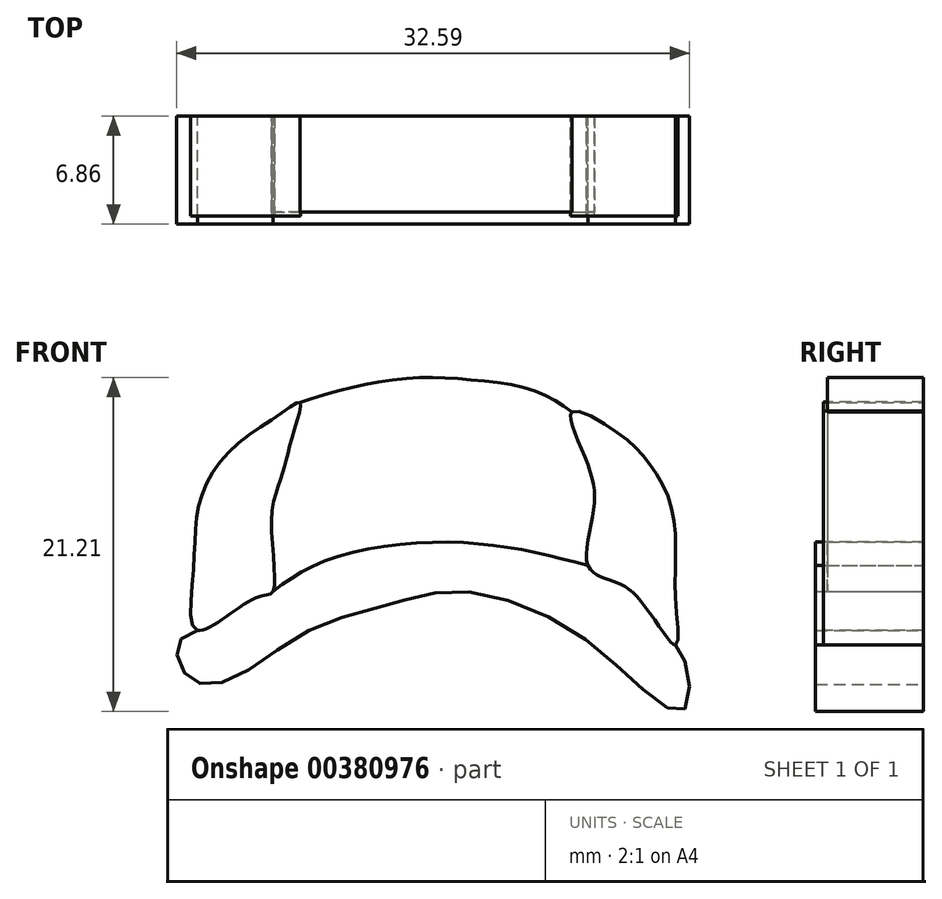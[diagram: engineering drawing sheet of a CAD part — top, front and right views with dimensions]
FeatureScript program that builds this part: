
annotation { "Feature Type Name" : "Feature", "Feature Type Description" : "" }
export const myFeature = defineFeature(function(context is Context, id is Id, definition is map)
    precondition{}
    {
        {
            var Q0;
            Q0=qCreatedBy(makeId("Front.planeOp"),FACE);
            var sketch = newSketch(context, id + "F0", { "sketchPlane" : qUnion([Q0])});
            skFitSpline(sketch, "E0", {"points": [v(-98.95, 24.46) * mm, v(-99.21, 28.23) * mm, v(-98.87, 32.42) * mm, v(-96.9, 35.84) * mm, v(-93.4, 38.41) * mm, v(-92.45, 38.92) * mm, v(-92.96, 36.61) * mm, v(-93.56, 34.39) * mm, v(-94.25, 31.48) * mm, v(-94.16, 26.95) * mm, v(-95.27, 26.52) * mm, v(-98.95, 24.46) * mm]});
            skFitSpline(sketch, "E1", {"points": [v(-75.17, 38.33) * mm, v(-74.23, 35.16) * mm, v(-73.8, 32.08) * mm, v(-74.14, 28.57) * mm, v(-72.69, 27.63) * mm, v(-70.89, 26.43) * mm, v(-68.58, 23.52) * mm, v(-68.58, 26.26) * mm, v(-68.58, 29.6) * mm, v(-69, 32.76) * mm, v(-70.46, 35.33) * mm, v(-72.43, 37.13) * mm, v(-75.17, 38.33) * mm]});
            skFitSpline(sketch, "E2", {"points": [v(-94.16, 26.95) * mm, v(-91, 28.83) * mm, v(-84.84, 30.03) * mm, v(-78.93, 29.68) * mm, v(-74.14, 28.57) * mm], "startDerivative": vector(13.27, 9.67) * mm, "endDerivative": vector(19.14, -5.1) * mm});
            skFitSpline(sketch, "E3", {"points": [v(-75.17, 38.33) * mm, v(-77.56, 39.7) * mm, v(-81.58, 40.38) * mm, v(-85.6, 40.46) * mm, v(-89.97, 39.7) * mm, v(-92.45, 38.92) * mm], "startDerivative": vector(-12.28, 8.74) * mm, "endDerivative": vector(-13.23, -4.52) * mm});
            skFitSpline(sketch, "E4", {"points": [v(-98.95, 24.46) * mm, v(-100.15, 23.7) * mm, v(-100.07, 22.24) * mm, v(-98.95, 21.13) * mm, v(-96.56, 21.47) * mm, v(-91.85, 24.46) * mm, v(-86.8, 26.09) * mm, v(-82.44, 26.95) * mm, v(-75.17, 24.46) * mm, v(-70.12, 20.27) * mm, v(-68.06, 19.42) * mm, v(-67.8, 21.9) * mm, v(-68.58, 23.52) * mm], "startDerivative": vector(-27, -10.61) * mm, "endDerivative": vector(-14.79, 21.62) * mm});
            skSolve(sketch);
        }
        {
            var Q0;
            {var subQ0=sQuery(id+"F0.wireOp",EDGE,"E0");var subQ1=makeQuery(id+"F0.imprint","INTERSECT",VERTEX,{"derivedFrom":[subQ0,sQuery(id+"F0.wireOp",EDGE,"E3")]});Q0=makeQuery(id+"F0.imprint","IMPRINT",FACE,{"disambiguationData":[TD([[makeQuery(id+"F0.imprint","IMPRINT",EDGE,{"disambiguationData":[TD([[subQ1,1.0]])],"derivedFrom":subQ0}),-1.0]])]});}
            var Q1;
            {var subQ0=sQuery(id+"F0.wireOp",EDGE,"E1");var subQ1=makeQuery(id+"F0.imprint","INTERSECT",VERTEX,{"derivedFrom":[subQ0,sQuery(id+"F0.wireOp",EDGE,"E2")]});Q1=makeQuery(id+"F0.imprint","IMPRINT",FACE,{"disambiguationData":[TD([[makeQuery(id+"F0.imprint","IMPRINT",EDGE,{"disambiguationData":[TD([[subQ1,1.0]])],"derivedFrom":subQ0}),1.0]])]});}
            extrude(context, id + "F1", {"entities" : qUnion([Q0, Q1]), "depth" : 6.35 * mm});
        }
        {
            var Q0;
            {var subQ0=sQuery(id+"F0.wireOp",EDGE,"E2");Q0=makeQuery(id+"F0.imprint","IMPRINT",FACE,{"disambiguationData":[TD([[makeQuery(id+"F0.imprint","IMPRINT",EDGE,{"derivedFrom":subQ0}),-1.0]])]});}
            extrude(context, id + "F2", {"entities" : qUnion([Q0]), "depth" : 6.86 * mm});
        }
        {
            var Q0;
            {var subQ0=sQuery(id+"F0.wireOp",EDGE,"E2");Q0=makeQuery(id+"F0.imprint","IMPRINT",FACE,{"disambiguationData":[TD([[makeQuery(id+"F0.imprint","IMPRINT",EDGE,{"derivedFrom":subQ0}),1.0]])]});}
            extrude(context, id + "F3", {"entities" : qUnion([Q0]), "depth" : 6.1 * mm});
        }
    });
